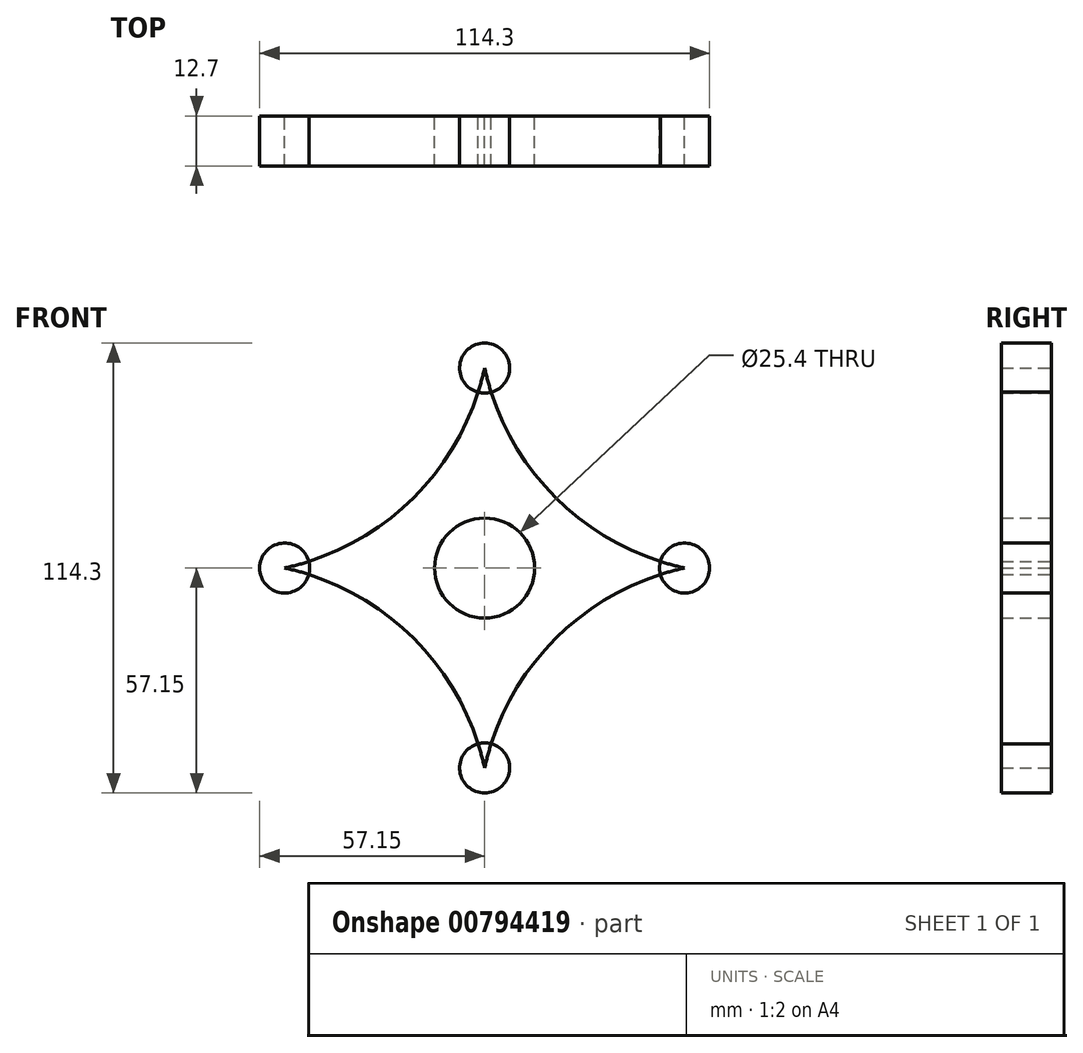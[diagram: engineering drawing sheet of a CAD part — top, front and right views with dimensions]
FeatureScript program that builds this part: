
annotation { "Feature Type Name" : "Feature", "Feature Type Description" : "" }
export const myFeature = defineFeature(function(context is Context, id is Id, definition is map)
    precondition{}
    {
        {
            var Q0;
            Q0=qCreatedBy(makeId("Front.planeOp"),FACE);
            var sketch = newSketch(context, id + "F0", { "sketchPlane" : qUnion([Q0])});
            skCircle(sketch, "E0", {"center": v(0, 0) * mm, "radius": 12.7 * mm});
            skCircle(sketch, "E1", {"center": v(50.8, 0) * mm, "radius": 6.35 * mm});
            skCircle(sketch, "E2", {"center": v(0, 50.8) * mm, "radius": 6.35 * mm});
            skCircle(sketch, "E3", {"center": v(-50.8, 0) * mm, "radius": 6.35 * mm});
            skCircle(sketch, "E4", {"center": v(0, -50.8) * mm, "radius": 6.35 * mm});
            skArc(sketch, "E5", {"start": v(-50.8, 0) * mm, "mid": v(-17.96, 17.96) * mm, "end": v(0, 50.8) * mm});
            skArc(sketch, "E6", {"start": v(0, 50.8) * mm, "mid": v(17.96, 17.96) * mm, "end": v(50.8, 0) * mm});
            skArc(sketch, "E7", {"start": v(0, -50.8) * mm, "mid": v(-17.96, -17.96) * mm, "end": v(-50.8, 0) * mm});
            skArc(sketch, "E8", {"start": v(50.8, 0) * mm, "mid": v(17.96, -17.96) * mm, "end": v(0, -50.8) * mm});
            skSolve(sketch);
        }
        {
            var Q0;
            Q0=makeQuery(id+"F0.imprint","IMPRINT",FACE,{"disambiguationData":[TD([[makeQuery(id+"F0.imprint","IMPRINT",EDGE,{"derivedFrom":sQuery(id+"F0.wireOp",EDGE,"E0")}),-1.0]])]});
            var Q1;
            {var subQ0=sQuery(id+"F0.wireOp",EDGE,"E5");var subQ1=sQuery(id+"F0.wireOp",EDGE,"E3");var subQ2=makeQuery(id+"F0.imprint","INTERSECT",VERTEX,{"derivedFrom":[subQ1,subQ0]});Q1=makeQuery(id+"F0.imprint","IMPRINT",FACE,{"disambiguationData":[TD([[makeQuery(id+"F0.imprint","IMPRINT",EDGE,{"disambiguationData":[TD([[subQ2,-1.0]])],"derivedFrom":subQ1}),1.0]])]});}
            var Q2;
            {var subQ0=sQuery(id+"F0.wireOp",EDGE,"E5");var subQ1=sQuery(id+"F0.wireOp",EDGE,"E2");var subQ2=makeQuery(id+"F0.imprint","INTERSECT",VERTEX,{"derivedFrom":[subQ1,subQ0]});Q2=makeQuery(id+"F0.imprint","IMPRINT",FACE,{"disambiguationData":[TD([[makeQuery(id+"F0.imprint","IMPRINT",EDGE,{"disambiguationData":[TD([[subQ2,1.0]])],"derivedFrom":subQ1}),1.0]])]});}
            var Q3;
            {var subQ0=sQuery(id+"F0.wireOp",EDGE,"E6");var subQ1=sQuery(id+"F0.wireOp",EDGE,"E1");var subQ2=makeQuery(id+"F0.imprint","INTERSECT",VERTEX,{"derivedFrom":[subQ1,subQ0]});Q3=makeQuery(id+"F0.imprint","IMPRINT",FACE,{"disambiguationData":[TD([[makeQuery(id+"F0.imprint","IMPRINT",EDGE,{"disambiguationData":[TD([[subQ2,1.0]])],"derivedFrom":subQ1}),1.0]])]});}
            var Q4;
            {var subQ0=sQuery(id+"F0.wireOp",EDGE,"E7");var subQ1=sQuery(id+"F0.wireOp",EDGE,"E4");var subQ2=makeQuery(id+"F0.imprint","INTERSECT",VERTEX,{"derivedFrom":[subQ1,subQ0]});Q4=makeQuery(id+"F0.imprint","IMPRINT",FACE,{"disambiguationData":[TD([[makeQuery(id+"F0.imprint","IMPRINT",EDGE,{"disambiguationData":[TD([[subQ2,-1.0]])],"derivedFrom":subQ1}),1.0]])]});}
            extrude(context, id + "F1", {"entities" : qUnion([Q0, Q1, Q2, Q3, Q4]), "depth" : 12.7 * mm, "offsetDistance" : 25.4 * mm});
        }
    });
